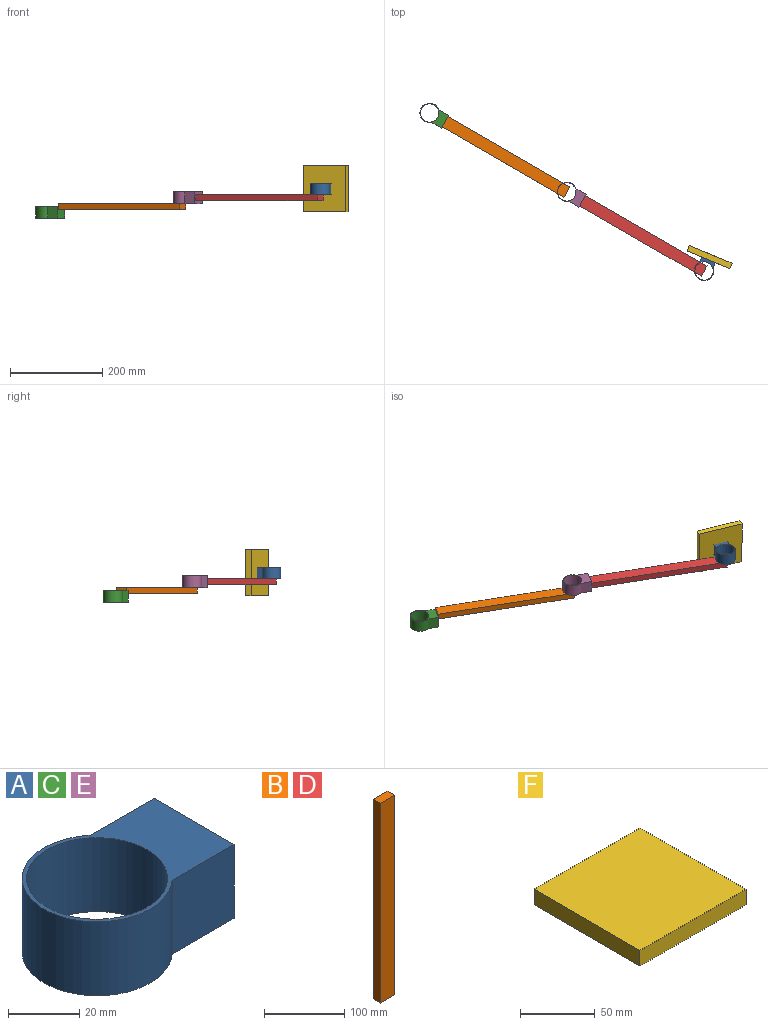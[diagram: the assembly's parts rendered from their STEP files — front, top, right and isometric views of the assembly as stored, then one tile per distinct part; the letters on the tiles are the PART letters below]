
ASSEMBLY  parts=6 mates=5
PART A: 7 faces, bbox 59.9x42.2x25.4 mm
  f0: cylinder r=21.08mm len=42.15mm, axis (0,0,-1), area 2450.5mm2, adj f1,f4,f5,f6
  f1: plane 25.4x24.55mm, normal (0,-1,0), area 623.5mm2, adj f0,f2,f5,f6
  f2: plane 31.73x25.4mm, normal (1,0,0), area 806mm2, adj f1,f4,f5,f6
  f3: cylinder r=19.81mm len=39.62mm, axis (0,0,-1), area 3161.9mm2, adj f5,f6
  f4: plane 25.4x25.4mm, normal (0,1,0), area 645.2mm2, adj f0,f2,f5,f6
  f5: plane 59.91x42.15mm, normal (0,0,1), area 796.1mm2, adj f0,f1,f2,f3,f4
  f6: plane 59.91x42.15mm, normal (0,0,-1), area 796.1mm2, adj f0,f1,f2,f3,f4
PART B: 6 faces, bbox 25.4x12.7x304.8 mm
  f0: plane 304.8x12.7mm, normal (-1,0,0), area 3871mm2, adj f1,f3,f4,f5
  f1: plane 304.8x25.4mm, normal (0,-1,0), area 7741.9mm2, adj f0,f2,f4,f5
  f2: plane 304.8x12.7mm, normal (1,0,0), area 3871mm2, adj f1,f3,f4,f5
  f3: plane 304.8x25.4mm, normal (0,1,0), area 7741.9mm2, adj f0,f2,f4,f5
  f4: plane 25.4x12.7mm, normal (0,0,1), area 322.6mm2, adj f0,f1,f2,f3
  f5: plane 25.4x12.7mm, normal (0,0,-1), area 322.6mm2, adj f0,f1,f2,f3
PART C: same geometry as A
PART D: same geometry as B
PART E: same geometry as A
PART F: 6 faces, bbox 100x100x12.7 mm
  f0: plane 100x12.7mm, normal (0,-1,0), area 1270mm2, adj f1,f3,f4,f5
  f1: plane 100x12.7mm, normal (1,0,0), area 1270mm2, adj f0,f2,f4,f5
  f2: plane 100x12.7mm, normal (0,1,0), area 1270mm2, adj f1,f3,f4,f5
  f3: plane 100x12.7mm, normal (-1,0,0), area 1270mm2, adj f0,f2,f4,f5
  f4: plane 100x100mm, normal (0,0,1), area 10000mm2, adj f0,f1,f2,f3
  f5: plane 100x100mm, normal (0,0,-1), area 10000mm2, adj f0,f1,f2,f3
PLACE A rot(axis=(0,0,1),67.6deg) t=(965.06,-811.54,249.59)mm
PLACE B rot(axis=(0.77,0.45,0.45),104.5deg) t=(403.32,-487.65,224.19)mm
PLACE C rot(axis=(0,0,-1),30deg) t=(369.5,-468.55,198.79)mm
PLACE D rot(axis=(-0.77,-0.45,0.45),104.5deg) t=(965.06,-811.54,243.24)mm
PLACE E rot(axis=(0,0,-1),30deg) t=(667.28,-640.05,230.54)mm
PLACE F rot(axis=(0.14,0.7,0.7),164.2deg) t=(974.68,-787.24,262.29)mm
MATE fastened F.f4 <-> A.f2  axis (0.38,0.92,0) through (979.53,-775.5,262.29)mm
MATE fastened D.f4 <-> E.f2  axis (-0.87,0.5,0) through (701.1,-659.14,243.24)mm
MATE ball A.f0 <-> D.f1  axis (0,0,-1) through (965.06,-811.54,249.59)mm
MATE revolute E.f0 <-> B.f3  axis (0,0,-1) through (667.28,-640.05,230.54)mm
MATE fastened B.f5 <-> C.f2  axis (-0.87,0.5,0) through (403.32,-487.65,224.19)mm
